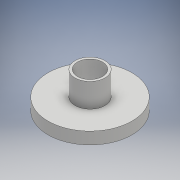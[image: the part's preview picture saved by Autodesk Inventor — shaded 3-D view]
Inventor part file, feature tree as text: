
AUTODESK INVENTOR PART (.ipt)
format: ipt  version: 2017 (Build 210142000, 142)  size: 105,984 bytes
history: native  units: mm
features: extrude x2, sketch x2
ambient origin geometry x8: Origin, YZ Plane, XZ Plane, XY Plane, X Axis, Y Axis, Z Axis, Center Point
bodies: Solide1 (feature_tree)
feature tree (4):
  extrude  "Extrusion1"  Depth=14.0mm
  extrude  "Extrusion2"  Depth=2.0mm TaperAngle=0.0deg
  sketch  "Esquisse1"
  sketch  "Esquisse2"
